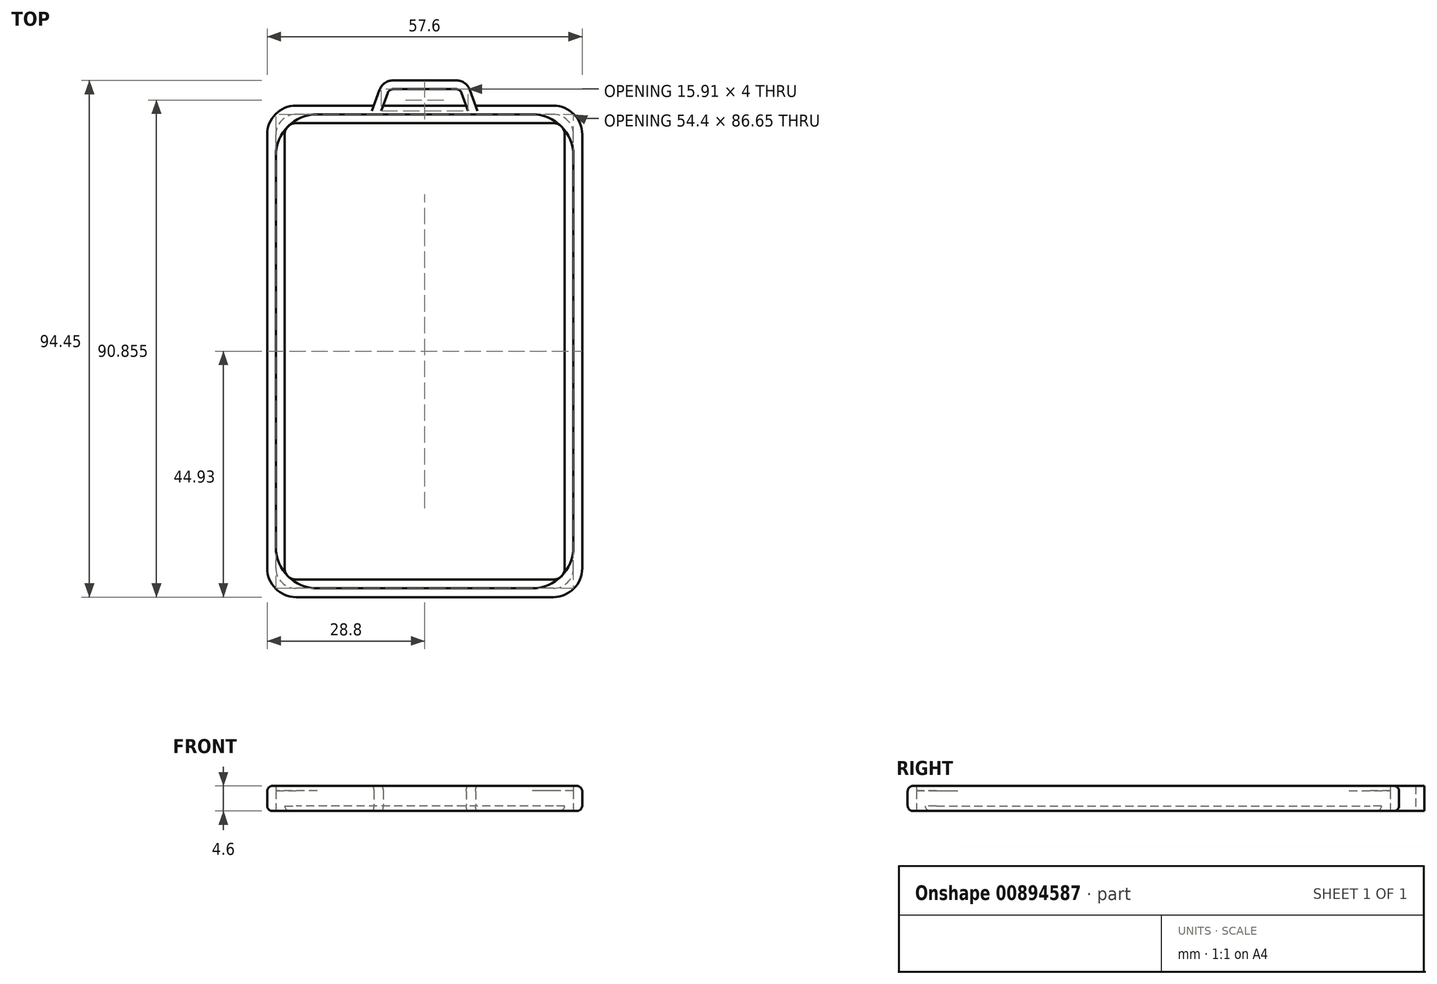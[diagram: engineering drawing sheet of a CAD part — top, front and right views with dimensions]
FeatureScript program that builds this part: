
annotation { "Feature Type Name" : "Feature", "Feature Type Description" : "" }
export const myFeature = defineFeature(function(context is Context, id is Id, definition is map)
    precondition{}
    {
        {
            var Q0;
            Q0=qCreatedBy(makeId("Top.planeOp"),FACE);
            var sketch = newSketch(context, id + "F0", { "sketchPlane" : qUnion([Q0])});
            skLineSegment(sketch, "E0.bottom", {"start": v(23.52, -43.13) * mm, "end": v(-23.52, -43.13) * mm});
            skLineSegment(sketch, "E0.top", {"start": v(23.52, 43.13) * mm, "end": v(-23.52, 43.13) * mm});
            skLineSegment(sketch, "E0.left", {"start": v(27, -39.64) * mm, "end": v(27, 39.64) * mm});
            skLineSegment(sketch, "E0.right", {"start": v(-27, -39.64) * mm, "end": v(-27, 39.64) * mm, "construction": true});
            skPoint(sketch, "E0.middle", {"position": v(0, 0) * mm});
            skPoint(sketch, "E1.visualSharp", {"position": v(-27, 43.13) * mm});
            skArc(sketch, "E1.filletArc", {"start": v(-23.52, 43.13) * mm, "mid": v(-25.98, 42.1) * mm, "end": v(-27, 39.64) * mm});
            skPoint(sketch, "E2.visualSharp", {"position": v(27, 43.13) * mm});
            skArc(sketch, "E2.filletArc", {"start": v(27, 39.64) * mm, "mid": v(25.98, 42.1) * mm, "end": v(23.52, 43.12) * mm});
            skPoint(sketch, "E3.visualSharp", {"position": v(27, -43.12) * mm});
            skArc(sketch, "E3.filletArc", {"start": v(23.52, -43.13) * mm, "mid": v(25.98, -42.1) * mm, "end": v(27, -39.64) * mm});
            skPoint(sketch, "E4.visualSharp", {"position": v(-27, -43.13) * mm});
            skArc(sketch, "E4.filletArc", {"start": v(-27, -39.64) * mm, "mid": v(-25.98, -42.1) * mm, "end": v(-23.52, -43.13) * mm});
            skArc(sketch, "E5.0", {"start": v(-27.2, -39.64) * mm, "mid": v(-26.12, -42.25) * mm, "end": v(-23.52, -43.33) * mm});
            skLineSegment(sketch, "E5.1", {"start": v(23.52, -43.33) * mm, "end": v(-23.52, -43.33) * mm});
            skLineSegment(sketch, "E5.2", {"start": v(-27.2, -39.64) * mm, "end": v(-27.2, 39.64) * mm});
            skArc(sketch, "E5.3", {"start": v(23.52, -43.33) * mm, "mid": v(26.12, -42.25) * mm, "end": v(27.2, -39.64) * mm});
            skArc(sketch, "E5.4", {"start": v(-23.52, 43.33) * mm, "mid": v(-26.12, 42.25) * mm, "end": v(-27.2, 39.64) * mm});
            skLineSegment(sketch, "E5.5", {"start": v(23.52, 43.33) * mm, "end": v(-23.52, 43.33) * mm});
            skArc(sketch, "E5.6", {"start": v(27.2, 39.64) * mm, "mid": v(26.12, 42.25) * mm, "end": v(23.52, 43.32) * mm});
            skLineSegment(sketch, "E5.7", {"start": v(27.2, -39.64) * mm, "end": v(27.2, 39.64) * mm});
            skArc(sketch, "E6.0", {"start": v(-28.8, -39.64) * mm, "mid": v(-27.25, -43.38) * mm, "end": v(-23.52, -44.93) * mm});
            skLineSegment(sketch, "E6.1", {"start": v(23.52, -44.93) * mm, "end": v(-23.52, -44.93) * mm});
            skLineSegment(sketch, "E6.2", {"start": v(-28.8, -39.64) * mm, "end": v(-28.8, 39.64) * mm});
            skArc(sketch, "E6.3", {"start": v(23.52, -44.93) * mm, "mid": v(27.25, -43.38) * mm, "end": v(28.8, -39.64) * mm});
            skArc(sketch, "E6.4", {"start": v(-23.52, 44.93) * mm, "mid": v(-27.25, 43.38) * mm, "end": v(-28.8, 39.64) * mm});
            skLineSegment(sketch, "E6.5", {"start": v(23.52, 44.93) * mm, "end": v(-23.52, 44.93) * mm});
            skArc(sketch, "E6.6", {"start": v(28.8, 39.64) * mm, "mid": v(27.25, 43.38) * mm, "end": v(23.52, 44.92) * mm});
            skLineSegment(sketch, "E6.7", {"start": v(28.8, -39.64) * mm, "end": v(28.8, 39.64) * mm});
            skSolve(sketch);
        }
        {
            var Q0;
            Q0=makeQuery(id+"F0.imprint","IMPRINT",FACE,{"disambiguationData":[TD([[makeQuery(id+"F0.imprint","IMPRINT",EDGE,{"derivedFrom":sQuery(id+"F0.wireOp",EDGE,"E5.0")}),-1.0]])]});
            extrude(context, id + "F1", {"entities" : qUnion([Q0]), "depth" : 2.8 * mm});
        }
        {
            var Q0;
            Q0=makeQuery(id+"F1.opExtrude","CAP_FACE",FACE,{"disambiguationData":[OSD([sQuery(id+"F0.wireOp",EDGE,"E5.0"),sQuery(id+"F0.wireOp",EDGE,"E5.1"),sQuery(id+"F0.wireOp",EDGE,"E5.2"),sQuery(id+"F0.wireOp",EDGE,"E5.3"),sQuery(id+"F0.wireOp",EDGE,"E5.4"),sQuery(id+"F0.wireOp",EDGE,"E5.5"),sQuery(id+"F0.wireOp",EDGE,"E5.6"),sQuery(id+"F0.wireOp",EDGE,"E5.7"),sQuery(id+"F0.wireOp",EDGE,"E6.0"),sQuery(id+"F0.wireOp",EDGE,"E6.1"),sQuery(id+"F0.wireOp",EDGE,"E6.2"),sQuery(id+"F0.wireOp",EDGE,"E6.3"),sQuery(id+"F0.wireOp",EDGE,"E6.4"),sQuery(id+"F0.wireOp",EDGE,"E6.5"),sQuery(id+"F0.wireOp",EDGE,"E6.6"),sQuery(id+"F0.wireOp",EDGE,"E6.7")])],"isStart":true});
            var sketch = newSketch(context, id + "F2", { "sketchPlane" : qUnion([Q0])});
            skArc(sketch, "E7.0.0", {"start": v(28.8, 39.64) * mm, "mid": v(27.25, 43.38) * mm, "end": v(23.52, 44.93) * mm});
            skLineSegment(sketch, "E7.0.1", {"start": v(23.52, 44.93) * mm, "end": v(-23.52, 44.93) * mm});
            skArc(sketch, "E7.0.2", {"start": v(-23.52, 44.93) * mm, "mid": v(-27.25, 43.38) * mm, "end": v(-28.8, 39.64) * mm});
            skLineSegment(sketch, "E7.0.3", {"start": v(-28.8, 39.64) * mm, "end": v(-28.8, -39.64) * mm});
            skArc(sketch, "E7.0.4", {"start": v(-28.8, -39.64) * mm, "mid": v(-27.25, -43.38) * mm, "end": v(-23.52, -44.93) * mm});
            skLineSegment(sketch, "E7.0.5", {"start": v(-23.52, -44.93) * mm, "end": v(23.52, -44.93) * mm});
            skArc(sketch, "E7.0.6", {"start": v(23.52, -44.93) * mm, "mid": v(27.25, -43.38) * mm, "end": v(28.8, -39.64) * mm});
            skLineSegment(sketch, "E7.0.7", {"start": v(28.8, -39.64) * mm, "end": v(28.8, 39.64) * mm});
            skArc(sketch, "E8.0", {"start": v(-25.6, 39.64) * mm, "mid": v(-24.99, 41.11) * mm, "end": v(-23.52, 41.73) * mm});
            skLineSegment(sketch, "E8.1", {"start": v(23.52, 41.73) * mm, "end": v(-23.52, 41.73) * mm});
            skLineSegment(sketch, "E8.2", {"start": v(-25.6, 39.64) * mm, "end": v(-25.6, -39.64) * mm});
            skArc(sketch, "E8.3", {"start": v(23.52, 41.73) * mm, "mid": v(24.99, 41.11) * mm, "end": v(25.6, 39.64) * mm});
            skArc(sketch, "E8.4", {"start": v(-23.52, -41.73) * mm, "mid": v(-24.99, -41.11) * mm, "end": v(-25.6, -39.64) * mm});
            skLineSegment(sketch, "E8.5", {"start": v(23.52, -41.73) * mm, "end": v(-23.52, -41.73) * mm});
            skArc(sketch, "E8.6", {"start": v(25.6, -39.64) * mm, "mid": v(24.99, -41.11) * mm, "end": v(23.52, -41.73) * mm});
            skLineSegment(sketch, "E8.7", {"start": v(25.6, 39.64) * mm, "end": v(25.6, -39.64) * mm});
            skSolve(sketch);
        }
        {
            var Q0;
            Q0=makeQuery(id+"F2.imprint","IMPRINT",FACE,{"disambiguationData":[TD([[makeQuery(id+"F2.imprint","IMPRINT",EDGE,{"derivedFrom":sQuery(id+"F2.wireOp",EDGE,"E8.0")}),1.0]])]});
            var Q1;
            Q1=makeQuery(id+"F2.imprint","IMPRINT",FACE,{"disambiguationData":[TD([[makeQuery(id+"F2.imprint","IMPRINT",EDGE,{"derivedFrom":sQuery(id+"F2.wireOp",EDGE,"E7.0.0")}),-1.0]])]});
            extrude(context, id + "F3", {"entities" : qUnion([Q0, Q1]), "operationType" : NewBodyOperationType.ADD, "depth" : 0.9 * mm});
        }
        {
            var Q0;
            Q0=makeQuery(id+"F1.opExtrude","CAP_FACE",FACE,{"disambiguationData":[OSD([sQuery(id+"F0.wireOp",EDGE,"E5.0"),sQuery(id+"F0.wireOp",EDGE,"E5.1"),sQuery(id+"F0.wireOp",EDGE,"E5.2"),sQuery(id+"F0.wireOp",EDGE,"E5.3"),sQuery(id+"F0.wireOp",EDGE,"E5.4"),sQuery(id+"F0.wireOp",EDGE,"E5.5"),sQuery(id+"F0.wireOp",EDGE,"E5.6"),sQuery(id+"F0.wireOp",EDGE,"E5.7"),sQuery(id+"F0.wireOp",EDGE,"E6.0"),sQuery(id+"F0.wireOp",EDGE,"E6.1"),sQuery(id+"F0.wireOp",EDGE,"E6.2"),sQuery(id+"F0.wireOp",EDGE,"E6.3"),sQuery(id+"F0.wireOp",EDGE,"E6.4"),sQuery(id+"F0.wireOp",EDGE,"E6.5"),sQuery(id+"F0.wireOp",EDGE,"E6.6"),sQuery(id+"F0.wireOp",EDGE,"E6.7")])],"isStart":false});
            var sketch = newSketch(context, id + "F4", { "sketchPlane" : qUnion([Q0])});
            skLineSegment(sketch, "E9.0", {"start": v(23.52, 43.33) * mm, "end": v(-23.52, 43.33) * mm});
            skLineSegment(sketch, "E10.0", {"start": v(-27.2, -39.64) * mm, "end": v(-27.2, 39.64) * mm});
            skLineSegment(sketch, "E11.0", {"start": v(27.2, -39.64) * mm, "end": v(27.2, 39.64) * mm});
            skLineSegment(sketch, "E12.0", {"start": v(23.52, -43.33) * mm, "end": v(-23.52, -43.33) * mm});
            skArc(sketch, "E13", {"start": v(-27.2, -35.78) * mm, "mid": v(-24.99, -41.11) * mm, "end": v(-19.65, -43.33) * mm});
            skArc(sketch, "E14", {"start": v(19.65, -43.33) * mm, "mid": v(24.99, -41.11) * mm, "end": v(27.2, -35.78) * mm});
            skArc(sketch, "E15", {"start": v(27.2, 35.78) * mm, "mid": v(24.99, 41.11) * mm, "end": v(19.65, 43.33) * mm});
            skArc(sketch, "E16", {"start": v(-19.65, 43.33) * mm, "mid": v(-24.99, 41.11) * mm, "end": v(-27.2, 35.78) * mm});
            skArc(sketch, "E17.0.0", {"start": v(23.52, -44.93) * mm, "mid": v(27.25, -43.38) * mm, "end": v(28.8, -39.64) * mm});
            skLineSegment(sketch, "E17.0.1", {"start": v(28.8, -39.64) * mm, "end": v(28.8, 39.64) * mm});
            skArc(sketch, "E17.0.2", {"start": v(28.8, 39.64) * mm, "mid": v(27.25, 43.38) * mm, "end": v(23.52, 44.93) * mm});
            skLineSegment(sketch, "E17.0.3", {"start": v(23.52, 44.93) * mm, "end": v(-23.52, 44.93) * mm});
            skArc(sketch, "E17.0.4", {"start": v(-23.52, 44.93) * mm, "mid": v(-27.25, 43.38) * mm, "end": v(-28.8, 39.64) * mm});
            skLineSegment(sketch, "E17.0.5", {"start": v(-28.8, 39.64) * mm, "end": v(-28.8, -39.64) * mm});
            skArc(sketch, "E17.0.6", {"start": v(-28.8, -39.64) * mm, "mid": v(-27.25, -43.38) * mm, "end": v(-23.52, -44.93) * mm});
            skLineSegment(sketch, "E17.0.7", {"start": v(-23.52, -44.93) * mm, "end": v(23.52, -44.93) * mm});
            skSolve(sketch);
        }
        {
            var Q0;
            Q0=makeQuery(id+"F4.imprint","IMPRINT",FACE,{"disambiguationData":[TD([[makeQuery(id+"F4.imprint","IMPRINT",EDGE,{"derivedFrom":sQuery(id+"F4.wireOp",EDGE,"E17.0.0")}),1.0]])]});
            var Q1;
            {var subQ2=sQuery(id+"F4.wireOp",EDGE,"E16");Q1=makeQuery(id+"F4.imprint","IMPRINT",FACE,{"disambiguationData":[TD([[makeQuery(id+"F4.imprint","IMPRINT",EDGE,{"derivedFrom":subQ2}),-1.0]])]});}
            var Q2;
            {var subQ2=sQuery(id+"F4.wireOp",EDGE,"E15");Q2=makeQuery(id+"F4.imprint","IMPRINT",FACE,{"disambiguationData":[TD([[makeQuery(id+"F4.imprint","IMPRINT",EDGE,{"derivedFrom":subQ2}),-1.0]])]});}
            var Q3;
            {var subQ2=sQuery(id+"F4.wireOp",EDGE,"E14");Q3=makeQuery(id+"F4.imprint","IMPRINT",FACE,{"disambiguationData":[TD([[makeQuery(id+"F4.imprint","IMPRINT",EDGE,{"derivedFrom":subQ2}),-1.0]])]});}
            var Q4;
            {var subQ2=sQuery(id+"F4.wireOp",EDGE,"E13");Q4=makeQuery(id+"F4.imprint","IMPRINT",FACE,{"disambiguationData":[TD([[makeQuery(id+"F4.imprint","IMPRINT",EDGE,{"derivedFrom":subQ2}),-1.0]])]});}
            extrude(context, id + "F5", {"entities" : qUnion([Q0, Q1, Q2, Q3, Q4]), "operationType" : NewBodyOperationType.ADD, "depth" : 0.9 * mm});
        }
        {
            var Q0;
            Q0=qCreatedBy(makeId("Top.planeOp"),FACE);
            var sketch = newSketch(context, id + "F6", { "sketchPlane" : qUnion([Q0])});
            skLineSegment(sketch, "E18", {"start": v(-7.6, 44.93) * mm, "end": v(-6.74, 47.27) * mm});
            skLineSegment(sketch, "E19", {"start": v(-5.8, 47.93) * mm, "end": v(5.8, 47.93) * mm});
            skLineSegment(sketch, "E20", {"start": v(6.74, 47.27) * mm, "end": v(7.6, 44.93) * mm});
            skLineSegment(sketch, "E21", {"start": v(0, 0) * mm, "end": v(0, 7.2) * mm, "construction": true});
            skPoint(sketch, "E22.visualSharp", {"position": v(-6.5, 47.93) * mm});
            skArc(sketch, "E22.filletArc", {"start": v(-5.8, 47.93) * mm, "mid": v(-6.37, 47.74) * mm, "end": v(-6.74, 47.27) * mm});
            skPoint(sketch, "E23.visualSharp", {"position": v(6.5, 47.93) * mm});
            skArc(sketch, "E23.filletArc", {"start": v(6.74, 47.27) * mm, "mid": v(6.37, 47.74) * mm, "end": v(5.8, 47.93) * mm});
            skLineSegment(sketch, "E24.0", {"start": v(8.24, 47.81) * mm, "end": v(9.3, 44.93) * mm});
            skLineSegment(sketch, "E24.1", {"start": v(-9.3, 44.93) * mm, "end": v(-8.24, 47.81) * mm});
            skArc(sketch, "E24.2", {"start": v(-5.8, 49.53) * mm, "mid": v(-7.3, 49.05) * mm, "end": v(-8.24, 47.81) * mm});
            skLineSegment(sketch, "E24.3", {"start": v(-5.8, 49.53) * mm, "end": v(5.8, 49.53) * mm});
            skArc(sketch, "E24.4", {"start": v(8.24, 47.81) * mm, "mid": v(7.3, 49.05) * mm, "end": v(5.8, 49.53) * mm});
            skLineSegment(sketch, "E25", {"start": v(9.3, 44.93) * mm, "end": v(7.6, 44.93) * mm});
            skLineSegment(sketch, "E26", {"start": v(-7.6, 44.93) * mm, "end": v(-9.3, 44.93) * mm});
            skSolve(sketch);
        }
        {
            var Q0;
            Q0=qSketchRegion(id+"F6",true);
            var Q1;
            Q1=makeQuery(id+"F5.opExtrude","CAP_FACE",FACE,{"disambiguationData":[OSD([sQuery(id+"F4.wireOp",EDGE,"E9.0"),sQuery(id+"F4.wireOp",EDGE,"E10.0"),sQuery(id+"F4.wireOp",EDGE,"E11.0"),sQuery(id+"F4.wireOp",EDGE,"E12.0"),sQuery(id+"F4.wireOp",EDGE,"E13"),sQuery(id+"F4.wireOp",EDGE,"E14"),sQuery(id+"F4.wireOp",EDGE,"E15"),sQuery(id+"F4.wireOp",EDGE,"E16"),sQuery(id+"F4.wireOp",EDGE,"E17.0.0"),sQuery(id+"F4.wireOp",EDGE,"E17.0.1"),sQuery(id+"F4.wireOp",EDGE,"E17.0.2"),sQuery(id+"F4.wireOp",EDGE,"E17.0.3"),sQuery(id+"F4.wireOp",EDGE,"E17.0.4"),sQuery(id+"F4.wireOp",EDGE,"E17.0.5"),sQuery(id+"F4.wireOp",EDGE,"E17.0.6"),sQuery(id+"F4.wireOp",EDGE,"E17.0.7")])],"isStart":false});
            var Q2;
            Q2=makeQuery(id+"F3.opExtrude","CAP_FACE",FACE,{"disambiguationData":[OSD([sQuery(id+"F2.wireOp",EDGE,"E7.0.0"),sQuery(id+"F2.wireOp",EDGE,"E7.0.1"),sQuery(id+"F2.wireOp",EDGE,"E7.0.2"),sQuery(id+"F2.wireOp",EDGE,"E7.0.3"),sQuery(id+"F2.wireOp",EDGE,"E7.0.4"),sQuery(id+"F2.wireOp",EDGE,"E7.0.5"),sQuery(id+"F2.wireOp",EDGE,"E7.0.6"),sQuery(id+"F2.wireOp",EDGE,"E7.0.7"),sQuery(id+"F2.wireOp",EDGE,"E8.0"),sQuery(id+"F2.wireOp",EDGE,"E8.1"),sQuery(id+"F2.wireOp",EDGE,"E8.2"),sQuery(id+"F2.wireOp",EDGE,"E8.3"),sQuery(id+"F2.wireOp",EDGE,"E8.4"),sQuery(id+"F2.wireOp",EDGE,"E8.5"),sQuery(id+"F2.wireOp",EDGE,"E8.6"),sQuery(id+"F2.wireOp",EDGE,"E8.7")])],"isStart":false});
            extrude(context, id + "F7", {"entities" : qUnion([Q0]), "operationType" : NewBodyOperationType.ADD, "endBound" : BoundingType.UP_TO_SURFACE, "endBoundEntityFace" : qUnion([Q1]), "depth" : 25 * mm, "hasSecondDirection" : true, "secondDirectionBound" : SecondDirectionBoundingType.UP_TO_SURFACE, "secondDirectionOppositeDirection" : true, "secondDirectionBoundEntityFace" : qUnion([Q2]), "secondDirectionDepth" : 25 * mm});
        }
        {
            var Q0;
            Q0=makeQuery(id+"F5.opExtrude","CAP_EDGE",EDGE,{"disambiguationData":[OSD([sQuery(id+"F4.wireOp",EDGE,"E17.0.5")])],"isStart":false});
            var Q1;
            Q1=makeQuery(id+"F3.opExtrude","CAP_EDGE",EDGE,{"disambiguationData":[OSD([sQuery(id+"F2.wireOp",EDGE,"E7.0.3")])],"isStart":false});
            var Q2;
            Q2=makeQuery(id+"F7.opExtrude","TWEAK_EDGE",EDGE,{"derivedFrom":[makeQuery(id+"F5.opExtrude","CAP_FACE",FACE,{"disambiguationData":[OSD([sQuery(id+"F4.wireOp",EDGE,"E9.0"),sQuery(id+"F4.wireOp",EDGE,"E10.0"),sQuery(id+"F4.wireOp",EDGE,"E11.0"),sQuery(id+"F4.wireOp",EDGE,"E12.0"),sQuery(id+"F4.wireOp",EDGE,"E13"),sQuery(id+"F4.wireOp",EDGE,"E14"),sQuery(id+"F4.wireOp",EDGE,"E15"),sQuery(id+"F4.wireOp",EDGE,"E16"),sQuery(id+"F4.wireOp",EDGE,"E17.0.0"),sQuery(id+"F4.wireOp",EDGE,"E17.0.1"),sQuery(id+"F4.wireOp",EDGE,"E17.0.2"),sQuery(id+"F4.wireOp",EDGE,"E17.0.3"),sQuery(id+"F4.wireOp",EDGE,"E17.0.4"),sQuery(id+"F4.wireOp",EDGE,"E17.0.5"),sQuery(id+"F4.wireOp",EDGE,"E17.0.6"),sQuery(id+"F4.wireOp",EDGE,"E17.0.7")])],"isStart":false}),makeQuery(id+"F6.imprint","IMPRINT",EDGE,{"derivedFrom":sQuery(id+"F6.wireOp",EDGE,"E18")})]});
            var Q3;
            Q3=makeQuery(id+"F7.opExtrude","TWEAK_EDGE",EDGE,{"derivedFrom":[makeQuery(id+"F3.opExtrude","CAP_FACE",FACE,{"disambiguationData":[OSD([sQuery(id+"F2.wireOp",EDGE,"E7.0.0"),sQuery(id+"F2.wireOp",EDGE,"E7.0.1"),sQuery(id+"F2.wireOp",EDGE,"E7.0.2"),sQuery(id+"F2.wireOp",EDGE,"E7.0.3"),sQuery(id+"F2.wireOp",EDGE,"E7.0.4"),sQuery(id+"F2.wireOp",EDGE,"E7.0.5"),sQuery(id+"F2.wireOp",EDGE,"E7.0.6"),sQuery(id+"F2.wireOp",EDGE,"E7.0.7"),sQuery(id+"F2.wireOp",EDGE,"E8.0"),sQuery(id+"F2.wireOp",EDGE,"E8.1"),sQuery(id+"F2.wireOp",EDGE,"E8.2"),sQuery(id+"F2.wireOp",EDGE,"E8.3"),sQuery(id+"F2.wireOp",EDGE,"E8.4"),sQuery(id+"F2.wireOp",EDGE,"E8.5"),sQuery(id+"F2.wireOp",EDGE,"E8.6"),sQuery(id+"F2.wireOp",EDGE,"E8.7")])],"isStart":false}),makeQuery(id+"F6.imprint","IMPRINT",EDGE,{"derivedFrom":sQuery(id+"F6.wireOp",EDGE,"E24.3")})]});
            var Q4;
            Q4=makeQuery(id+"F7.opExtrude","TWEAK_EDGE",EDGE,{"derivedFrom":[makeQuery(id+"F5.opExtrude","CAP_FACE",FACE,{"disambiguationData":[OSD([sQuery(id+"F4.wireOp",EDGE,"E9.0"),sQuery(id+"F4.wireOp",EDGE,"E10.0"),sQuery(id+"F4.wireOp",EDGE,"E11.0"),sQuery(id+"F4.wireOp",EDGE,"E12.0"),sQuery(id+"F4.wireOp",EDGE,"E13"),sQuery(id+"F4.wireOp",EDGE,"E14"),sQuery(id+"F4.wireOp",EDGE,"E15"),sQuery(id+"F4.wireOp",EDGE,"E16"),sQuery(id+"F4.wireOp",EDGE,"E17.0.0"),sQuery(id+"F4.wireOp",EDGE,"E17.0.1"),sQuery(id+"F4.wireOp",EDGE,"E17.0.2"),sQuery(id+"F4.wireOp",EDGE,"E17.0.3"),sQuery(id+"F4.wireOp",EDGE,"E17.0.4"),sQuery(id+"F4.wireOp",EDGE,"E17.0.5"),sQuery(id+"F4.wireOp",EDGE,"E17.0.6"),sQuery(id+"F4.wireOp",EDGE,"E17.0.7")])],"isStart":false}),makeQuery(id+"F6.imprint","IMPRINT",EDGE,{"derivedFrom":sQuery(id+"F6.wireOp",EDGE,"E24.3")})]});
            var Q5;
            {var subQ0=sQuery(id+"F2.wireOp",EDGE,"E7.0.5");Q5=makeQuery(id+"F7.boolean.opBoolean","SPLIT",EDGE,{"disambiguationData":[TD([makeQuery(id+"F7.opExtrude","SWEPT_FACE",FACE,{"disambiguationData":[OSD([sQuery(id+"F6.wireOp",EDGE,"E18")])]})])],"derivedFrom":makeQuery(id+"F3.opExtrude","CAP_EDGE",EDGE,{"disambiguationData":[OSD([subQ0])],"isStart":false})});}
            var Q6;
            {var subQ4=sQuery(id+"F4.wireOp",EDGE,"E17.0.3");Q6=makeQuery(id+"F7.boolean.opBoolean","SPLIT",EDGE,{"disambiguationData":[TD([makeQuery(id+"F7.opExtrude","SWEPT_FACE",FACE,{"disambiguationData":[OSD([sQuery(id+"F6.wireOp",EDGE,"E18")])]})])],"derivedFrom":makeQuery(id+"F5.opExtrude","CAP_EDGE",EDGE,{"disambiguationData":[OSD([subQ4])],"isStart":false})});}
            var Q7;
            Q7=makeQuery(id+"F7.opExtrude","TWEAK_EDGE",EDGE,{"derivedFrom":[makeQuery(id+"F3.opExtrude","CAP_FACE",FACE,{"disambiguationData":[OSD([sQuery(id+"F2.wireOp",EDGE,"E7.0.0"),sQuery(id+"F2.wireOp",EDGE,"E7.0.1"),sQuery(id+"F2.wireOp",EDGE,"E7.0.2"),sQuery(id+"F2.wireOp",EDGE,"E7.0.3"),sQuery(id+"F2.wireOp",EDGE,"E7.0.4"),sQuery(id+"F2.wireOp",EDGE,"E7.0.5"),sQuery(id+"F2.wireOp",EDGE,"E7.0.6"),sQuery(id+"F2.wireOp",EDGE,"E7.0.7"),sQuery(id+"F2.wireOp",EDGE,"E8.0"),sQuery(id+"F2.wireOp",EDGE,"E8.1"),sQuery(id+"F2.wireOp",EDGE,"E8.2"),sQuery(id+"F2.wireOp",EDGE,"E8.3"),sQuery(id+"F2.wireOp",EDGE,"E8.4"),sQuery(id+"F2.wireOp",EDGE,"E8.5"),sQuery(id+"F2.wireOp",EDGE,"E8.6"),sQuery(id+"F2.wireOp",EDGE,"E8.7")])],"isStart":false}),makeQuery(id+"F6.imprint","IMPRINT",EDGE,{"derivedFrom":sQuery(id+"F6.wireOp",EDGE,"E19")})]});
            var Q8;
            Q8=makeQuery(id+"F3.opExtrude","CAP_EDGE",EDGE,{"disambiguationData":[OSD([sQuery(id+"F2.wireOp",EDGE,"E8.2")])],"isStart":false});
            fillet(context, id + "F8", {"entities" : qUnion([Q0, Q1, Q2, Q3, Q4, Q5, Q6, Q7, Q8]), "radius" : 1 * mm, "tangentPropagation" : true, "allowEdgeOverflow" : false});
        }
    });
